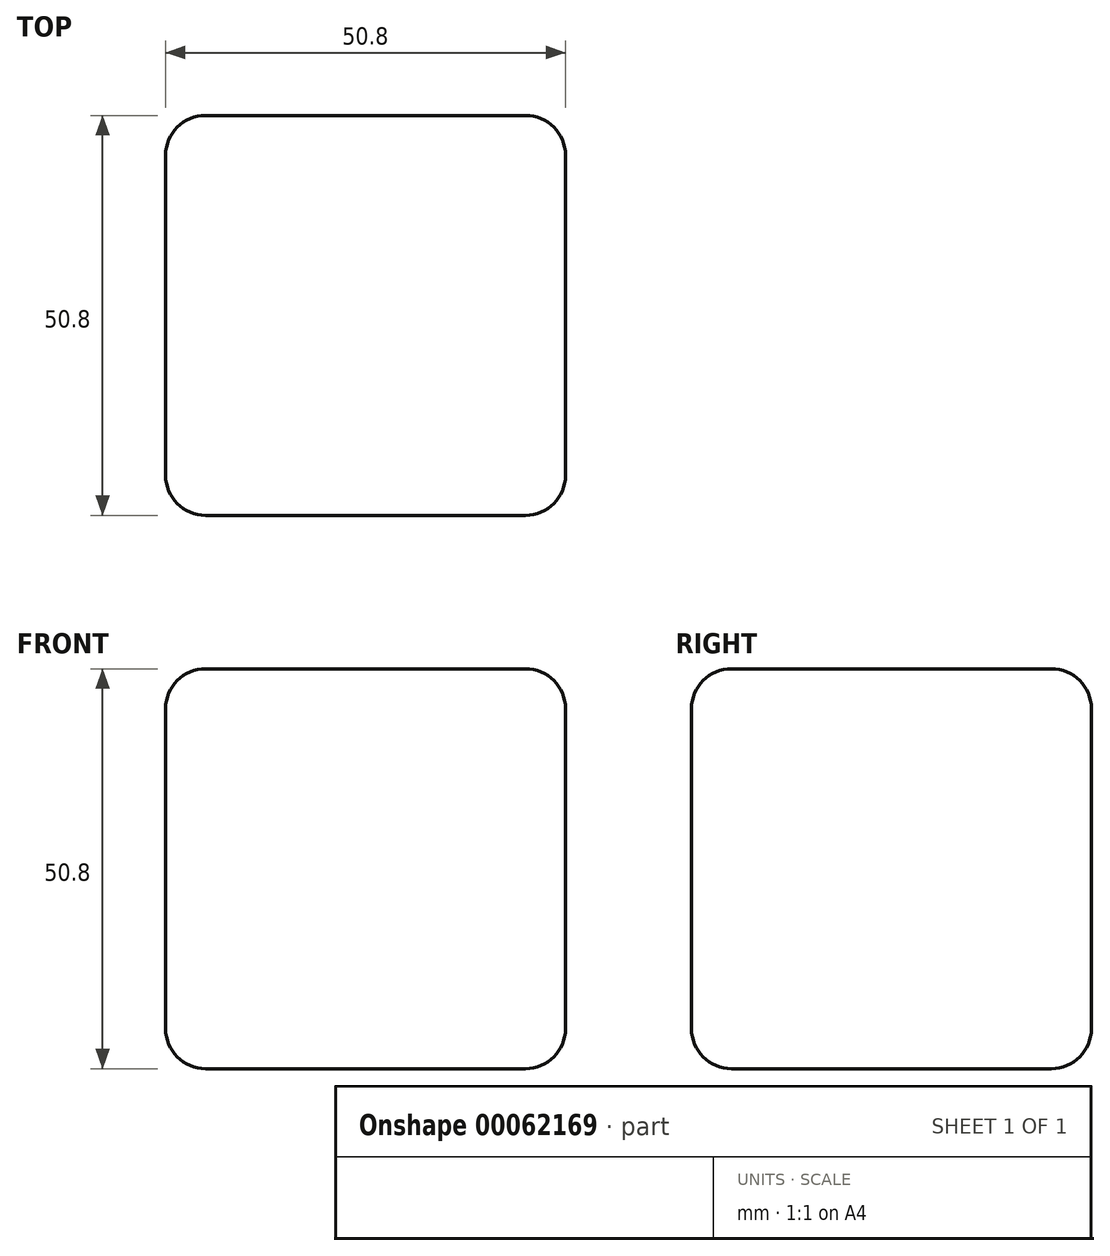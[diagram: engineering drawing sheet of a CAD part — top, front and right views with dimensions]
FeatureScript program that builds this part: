
annotation { "Feature Type Name" : "Feature", "Feature Type Description" : "" }
export const myFeature = defineFeature(function(context is Context, id is Id, definition is map)
    precondition{}
    {
        {
            var Q0;
            Q0=qCreatedBy(makeId("Top.planeOp"),FACE);
            var sketch = newSketch(context, id + "F0", { "sketchPlane" : qUnion([Q0])});
            skLineSegment(sketch, "E0", {"start": v(-20.7, 40.39) * mm, "end": v(30.1, 40.39) * mm});
            skLineSegment(sketch, "E1", {"start": v(30.1, 40.39) * mm, "end": v(30.1, -10.41) * mm});
            skLineSegment(sketch, "E2", {"start": v(-20.7, -10.41) * mm, "end": v(-20.7, 40.39) * mm});
            skLineSegment(sketch, "E3", {"start": v(30.1, -10.41) * mm, "end": v(-20.7, -10.41) * mm});
            skSolve(sketch);
        }
        {
            var Q0;
            Q0=makeQuery(id+"F0.imprint","IMPRINT",FACE,{"disambiguationData":[TD([[makeQuery(id+"F0.imprint","IMPRINT",EDGE,{"derivedFrom":sQuery(id+"F0.wireOp",EDGE,"E0")}),-1.0]])]});
            extrude(context, id + "F1", {"entities" : qUnion([Q0]), "depth" : 50.8 * mm});
        }
        {
            var Q0;
            Q0=makeQuery(id+"F1.opExtrude","SWEPT_EDGE",EDGE,{"disambiguationData":[OSD([sQuery(id+"F0.wireOp",EDGE,"E0"),sQuery(id+"F0.wireOp",EDGE,"E1")])]});
            var Q1;
            Q1=makeQuery(id+"F1.opExtrude","CAP_EDGE",EDGE,{"disambiguationData":[OSD([sQuery(id+"F0.wireOp",EDGE,"E0")])],"isStart":false});
            var Q2;
            Q2=makeQuery(id+"F1.opExtrude","SWEPT_FACE",FACE,{"disambiguationData":[OSD([sQuery(id+"F0.wireOp",EDGE,"E2")])]});
            var Q3;
            Q3=makeQuery(id+"F1.opExtrude","CAP_EDGE",EDGE,{"disambiguationData":[OSD([sQuery(id+"F0.wireOp",EDGE,"E0")])],"isStart":true});
            var Q4;
            Q4=makeQuery(id+"F1.opExtrude","CAP_EDGE",EDGE,{"disambiguationData":[OSD([sQuery(id+"F0.wireOp",EDGE,"E1")])],"isStart":true});
            var Q5;
            Q5=makeQuery(id+"F1.opExtrude","SWEPT_EDGE",EDGE,{"disambiguationData":[OSD([sQuery(id+"F0.wireOp",EDGE,"E1"),sQuery(id+"F0.wireOp",EDGE,"E3")])]});
            var Q6;
            Q6=makeQuery(id+"F1.opExtrude","CAP_EDGE",EDGE,{"disambiguationData":[OSD([sQuery(id+"F0.wireOp",EDGE,"E3")])],"isStart":true});
            var Q7;
            Q7=makeQuery(id+"F1.opExtrude","CAP_EDGE",EDGE,{"disambiguationData":[OSD([sQuery(id+"F0.wireOp",EDGE,"E1")])],"isStart":false});
            var Q8;
            Q8=makeQuery(id+"F1.opExtrude","CAP_EDGE",EDGE,{"disambiguationData":[OSD([sQuery(id+"F0.wireOp",EDGE,"E3")])],"isStart":false});
            fillet(context, id + "F2", {"entities" : qUnion([Q0, Q1, Q2, Q3, Q4, Q5, Q6, Q7, Q8]), "radius" : 5.08 * mm, "tangentPropagation" : true, "allowEdgeOverflow" : false});
        }
    });
